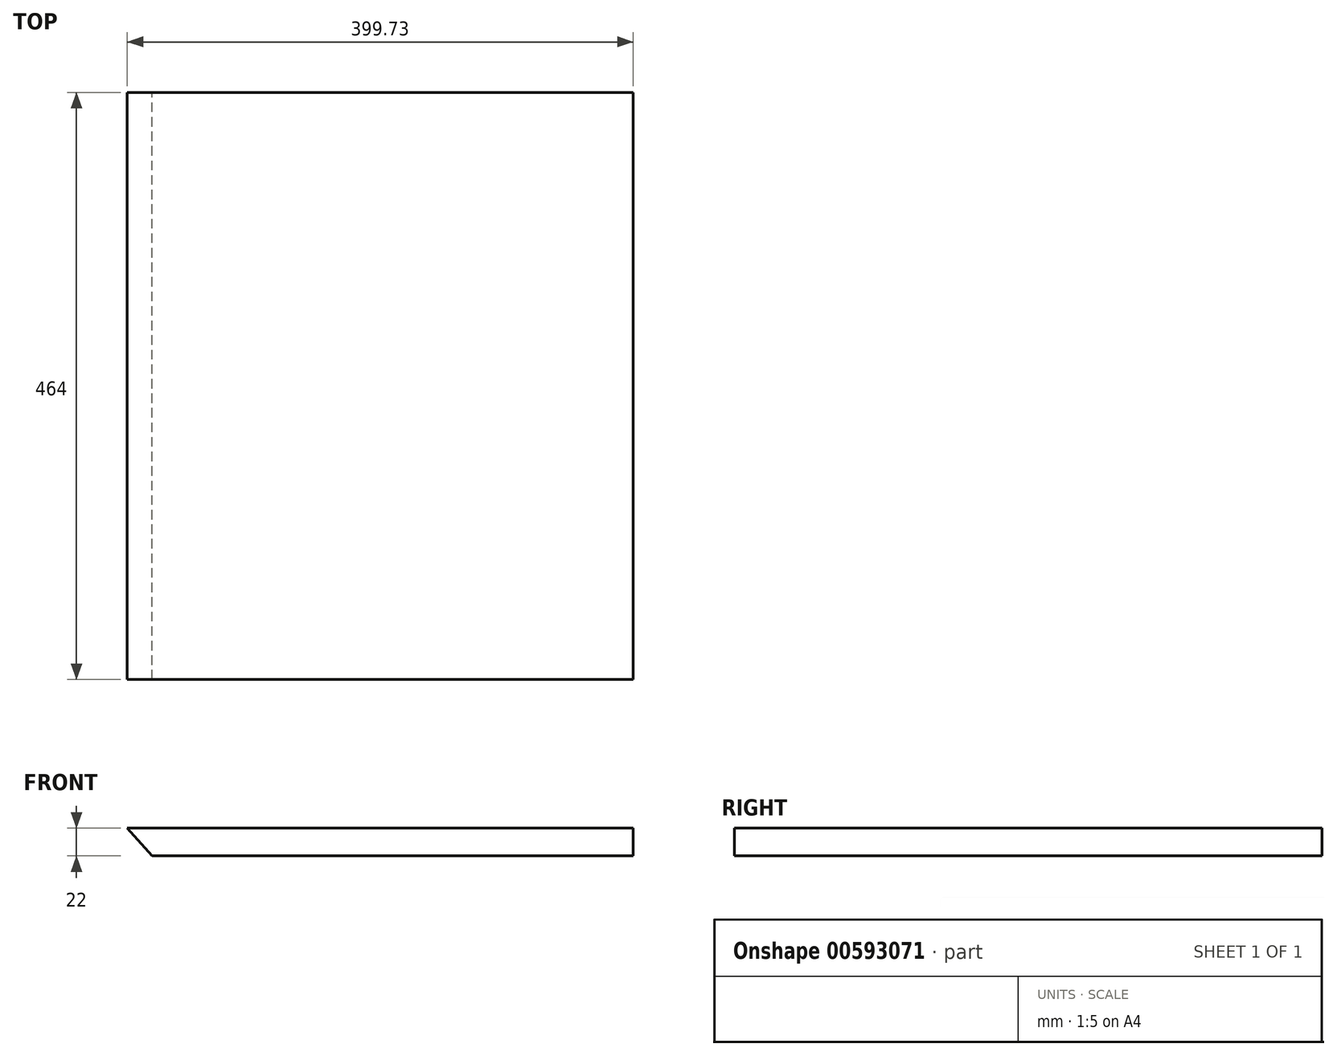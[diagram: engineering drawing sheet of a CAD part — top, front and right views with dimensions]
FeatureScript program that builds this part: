
annotation { "Feature Type Name" : "Feature", "Feature Type Description" : "" }
export const myFeature = defineFeature(function(context is Context, id is Id, definition is map)
    precondition{}
    {
        {
            var Q0;
            Q0=qCreatedBy(makeId("Front.planeOp"),FACE);
            var sketch = newSketch(context, id + "F0", { "sketchPlane" : qUnion([Q0])});
            skLineSegment(sketch, "E0.bottom", {"start": v(-190, 0) * mm, "end": v(190, 0) * mm});
            skLineSegment(sketch, "E0.top", {"start": v(-190, -22) * mm, "end": v(190, -22) * mm});
            skLineSegment(sketch, "E0.right", {"start": v(190, 0) * mm, "end": v(190, -22) * mm});
            skLineSegment(sketch, "E1", {"start": v(-190, -22) * mm, "end": v(-209.73, 0) * mm});
            skLineSegment(sketch, "E2", {"start": v(-209.73, 0) * mm, "end": v(-190, 0) * mm});
            skSolve(sketch);
        }
        {
            var Q0;
            Q0=makeQuery(id+"F0.imprint","IMPRINT",FACE,{"disambiguationData":[TD([[makeQuery(id+"F0.imprint","IMPRINT",EDGE,{"derivedFrom":sQuery(id+"F0.wireOp",EDGE,"E0.bottom")}),-1.0]])]});
            extrude(context, id + "F1", {"entities" : qUnion([Q0]), "depth" : 464 * mm, "offsetDistance" : 25 * mm});
        }
    });
